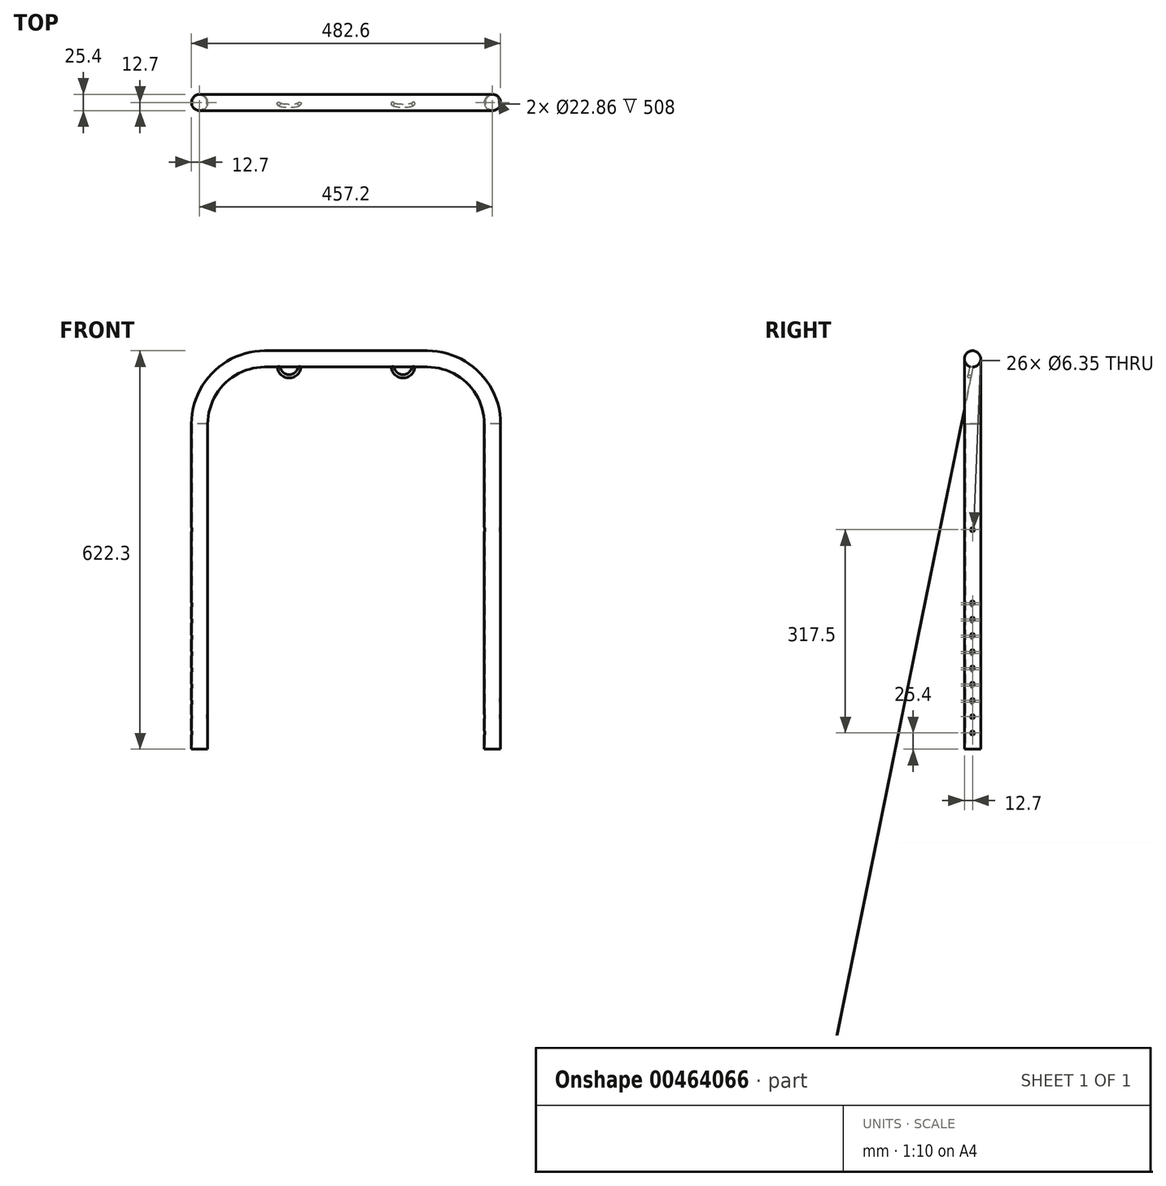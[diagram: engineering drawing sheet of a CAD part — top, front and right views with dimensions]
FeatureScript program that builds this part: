
annotation { "Feature Type Name" : "Feature", "Feature Type Description" : "" }
export const myFeature = defineFeature(function(context is Context, id is Id, definition is map)
    precondition{}
    {
        {
            var Q0;
            Q0=qCreatedBy(makeId("Front.planeOp"),FACE);
            var sketch = newSketch(context, id + "F0", { "sketchPlane" : qUnion([Q0])});
            skLineSegment(sketch, "E0", {"start": v(0, 0) * mm, "end": v(-228.6, 0) * mm});
            skLineSegment(sketch, "E1", {"start": v(-228.6, 0) * mm, "end": v(-228.6, 508) * mm});
            skLineSegment(sketch, "E2", {"start": v(0, 0) * mm, "end": v(0, 609.6) * mm});
            skLineSegment(sketch, "E3", {"start": v(0, 609.6) * mm, "end": v(-127, 609.6) * mm});
            skArc(sketch, "E4", {"start": v(-127, 609.6) * mm, "mid": v(-198.84, 579.84) * mm, "end": v(-228.6, 508) * mm});
            skSolve(sketch);
        }
        {
            var Q0;
            Q0=qCreatedBy(makeId("Top.planeOp"),FACE);
            var sketch = newSketch(context, id + "F1", { "sketchPlane" : qUnion([Q0])});
            skLineSegment(sketch, "E5", {"start": v(0, 0) * mm, "end": v(-228.6, 0) * mm});
            skCircle(sketch, "E6", {"center": v(-228.6, 0) * mm, "radius": 12.7 * mm});
            skSolve(sketch);
        }
        {
            var Q0;
            Q0=makeQuery(id+"F1.imprint","IMPRINT",FACE,{"disambiguationData":[TD([[makeQuery(id+"F1.imprint","IMPRINT",EDGE,{"derivedFrom":sQuery(id+"F1.wireOp",EDGE,"E6")}),1.0]])]});
            var Q1;
            Q1=sQuery(id+"F0.wireOp",EDGE,"E1");
            var Q2;
            Q2=sQuery(id+"F0.wireOp",EDGE,"E4");
            var Q3;
            Q3=sQuery(id+"F0.wireOp",EDGE,"E3");
            sweep(context, id + "F2", {"profiles" : qUnion([Q0]), "path" : qUnion([Q1, Q2, Q3])});
        }
        {
            var Q0;
            Q0=makeQuery(id+"F2.opSweep","SWEPT_BODY",BODY,{"disambiguationData":[OSD([sQuery(id+"F0.wireOp",EDGE,"E3"),sQuery(id+"F1.wireOp",EDGE,"E6")])]});
            var Q1;
            Q1=qCreatedBy(makeId("Right.planeOp"),FACE);
            mirror(context, id + "F3", {"operationType" : NewBodyOperationType.ADD, "entities" : qUnion([Q0]), "mirrorPlane" : qUnion([Q1])});
        }
        {
            var Q0;
            Q0=qCreatedBy(makeId("Right.planeOp"),FACE);
            cPlane(context, id + "F4", {"entities" : qUnion([Q0]), "cplaneType" : CPlaneType.OFFSET, "offset" : 228.6 * mm, "width" : 152.4 * mm, "height" : 152.4 * mm});
        }
        {
            var Q0;
            Q0=qCreatedBy(id+"F4.planeOp",FACE);
            cPlane(context, id + "F5", {"entities" : qUnion([Q0]), "cplaneType" : CPlaneType.OFFSET, "offset" : 6.35 * mm, "oppositeDirection" : true, "width" : 152.4 * mm, "height" : 152.4 * mm});
        }
        {
            var Q0;
            Q0=qCreatedBy(id+"F5.planeOp",FACE);
            var sketch = newSketch(context, id + "F6", { "sketchPlane" : qUnion([Q0])});
            skLineSegment(sketch, "E7", {"start": v(0, 0) * mm, "end": v(0, 50.8) * mm});
            skCircle(sketch, "E8", {"center": v(0, 50.8) * mm, "radius": 3.18 * mm});
            skSolve(sketch);
        }
        {
            var Q0;
            Q0 = qSketchRegion(id + "F6", true);
            extrude(context, id + "F7", {"entities" : qUnion([Q0]), "operationType" : NewBodyOperationType.REMOVE, "oppositeDirection" : true, "depth" : 601.98 * mm, "hasSecondDirection" : true, "secondDirectionOppositeDirection" : false, "secondDirectionDepth" : 101.6 * mm});
        }
        {
            var Q0;
            Q0=qCreatedBy(id+"F4.planeOp",FACE);
            var sketch = newSketch(context, id + "F8", { "sketchPlane" : qUnion([Q0])});
            skLineSegment(sketch, "E9", {"start": v(0, 0) * mm, "end": v(0, 342.9) * mm});
            skCircle(sketch, "E10", {"center": v(0, 342.9) * mm, "radius": 3.18 * mm});
            skSolve(sketch);
        }
        {
            var Q0;
            Q0 = qSketchRegion(id + "F8", true);
            extrude(context, id + "F9", {"entities" : qUnion([Q0]), "operationType" : NewBodyOperationType.REMOVE, "depth" : 19.05 * mm, "hasSecondDirection" : true, "secondDirectionOppositeDirection" : true, "secondDirectionDepth" : 840.74 * mm});
        }
        {
            var Q0;
            Q0=qCreatedBy(id+"F4.planeOp",FACE);
            var sketch = newSketch(context, id + "F10", { "sketchPlane" : qUnion([Q0])});
            skCircle(sketch, "E11", {"center": v(0, 25.4) * mm, "radius": 3.18 * mm});
            skSolve(sketch);
        }
        {
            var Q0;
            Q0 = qSketchRegion(id + "F10", true);
            extrude(context, id + "F11", {"entities" : qUnion([Q0]), "operationType" : NewBodyOperationType.REMOVE, "depth" : 19.05 * mm, "hasSecondDirection" : true, "secondDirectionOppositeDirection" : true, "secondDirectionDepth" : 693.42 * mm, "offsetDistance" : 25.4 * mm});
        }
        {
            var Q0;
            Q0=qCreatedBy(makeId("Top.planeOp"),FACE);
            cPlane(context, id + "F12", {"entities" : qUnion([Q0]), "cplaneType" : CPlaneType.OFFSET, "offset" : 596.9 * mm, "width" : 152.4 * mm, "height" : 152.4 * mm});
        }
        {
            var Q0;
            Q0=qCreatedBy(makeId("Right.planeOp"),FACE);
            var sketch = newSketch(context, id + "F13", { "sketchPlane" : qUnion([Q0])});
            skLineSegment(sketch, "E12", {"start": v(0, 594.75) * mm, "end": v(-58.05, 606.55) * mm});
            skLineSegment(sketch, "E13", {"start": v(0, 594.75) * mm, "end": v(13.15, 659.45) * mm});
            skSolve(sketch);
        }
        {
            var Q0;
            Q0=qCreatedBy(id+"F12.planeOp",FACE);
            var Q1;
            Q1=sQuery(id+"F13.wireOp",EDGE,"E12");
            cPlane(context, id + "F14", {"entities" : qUnion([Q0, Q1]), "cplaneType" : CPlaneType.LINE_ANGLE, "offset" : 25.4 * mm, "angle" : 0 * degree, "width" : 152.4 * mm, "height" : 152.4 * mm});
        }
        {
            var Q0;
            Q0=qCreatedBy(makeId("Front.planeOp"),FACE);
            var Q1;
            Q1=sQuery(id+"F13.wireOp",EDGE,"E13");
            cPlane(context, id + "F15", {"entities" : qUnion([Q0, Q1]), "cplaneType" : CPlaneType.LINE_ANGLE, "offset" : 25.4 * mm, "angle" : 0 * degree, "width" : 152.4 * mm, "height" : 152.4 * mm});
        }
        {
            var Q0;
            Q0=qCreatedBy(id+"F15.planeOp",FACE);
            var sketch = newSketch(context, id + "F16", { "sketchPlane" : qUnion([Q0])});
            skLineSegment(sketch, "E14", {"start": v(0, 585.75) * mm, "end": v(88.9, 585.75) * mm});
            skLineSegment(sketch, "E15", {"start": v(0, 585.75) * mm, "end": v(-88.9, 585.75) * mm});
            skCircle(sketch, "E16", {"center": v(88.9, 585.75) * mm, "radius": 15.88 * mm});
            skCircle(sketch, "E17", {"center": v(-88.9, 585.75) * mm, "radius": 15.88 * mm});
            skLineSegment(sketch, "E18", {"start": v(0, 585.75) * mm, "end": v(73.03, 585.75) * mm});
            skSolve(sketch);
        }
        {
            var Q0;
            Q0=qCreatedBy(id+"F14.planeOp",FACE);
            var sketch = newSketch(context, id + "F17", { "sketchPlane" : qUnion([Q0])});
            skLineSegment(sketch, "E19", {"start": v(0, 120.77) * mm, "end": v(-73.03, 120.77) * mm});
            skLineSegment(sketch, "E20", {"start": v(0, 120.77) * mm, "end": v(73.03, 120.77) * mm});
            skCircle(sketch, "E21", {"center": v(-73.03, 120.77) * mm, "radius": 2.54 * mm});
            skCircle(sketch, "E22", {"center": v(73.03, 120.77) * mm, "radius": 2.54 * mm});
            skSolve(sketch);
        }
        {
            var Q0;
            Q0=makeQuery(id+"F17.imprint","IMPRINT",FACE,{"disambiguationData":[TD([[makeQuery(id+"F17.imprint","IMPRINT",EDGE,{"derivedFrom":sQuery(id+"F17.wireOp",EDGE,"E21")}),1.0]])]});
            var Q1;
            Q1=sQuery(id+"F16.wireOp",EDGE,"E16");
            sweep(context, id + "F18", {"operationType" : NewBodyOperationType.ADD, "profiles" : qUnion([Q0]), "path" : qUnion([Q1])});
        }
        {
            var Q0;
            Q0=makeQuery(id+"F17.imprint","IMPRINT",FACE,{"disambiguationData":[TD([[makeQuery(id+"F17.imprint","IMPRINT",EDGE,{"derivedFrom":sQuery(id+"F17.wireOp",EDGE,"E22")}),1.0]])]});
            var Q1;
            Q1=sQuery(id+"F16.wireOp",EDGE,"E17");
            sweep(context, id + "F19", {"operationType" : NewBodyOperationType.ADD, "profiles" : qUnion([Q0]), "path" : qUnion([Q1])});
        }
        {
            var Q0;
            Q0=qCreatedBy(makeId("Top.planeOp"),FACE);
            var sketch = newSketch(context, id + "F20", { "sketchPlane" : qUnion([Q0])});
            skLineSegment(sketch, "E23", {"start": v(0, 0) * mm, "end": v(228.6, 0) * mm});
            skCircle(sketch, "E24", {"center": v(228.6, 0) * mm, "radius": 11.43 * mm});
            skLineSegment(sketch, "E25", {"start": v(0, 0) * mm, "end": v(0, 93.67) * mm});
            skCircle(sketch, "E26.MirrorC", {"center": v(-228.6, 0) * mm, "radius": 11.43 * mm});
            skSolve(sketch);
        }
        {
            var Q0;
            Q0 = qSketchRegion(id + "F20", true);
            extrude(context, id + "F21", {"entities" : qUnion([Q0]), "operationType" : NewBodyOperationType.REMOVE, "depth" : 508 * mm, "offsetDistance" : 25.4 * mm});
        }
        {
            var Q0;
            Q0=qCreatedBy(id+"F4.planeOp",FACE);
            var sketch = newSketch(context, id + "F22", { "sketchPlane" : qUnion([Q0])});
            skLineSegment(sketch, "E27", {"start": v(0, 0) * mm, "end": v(0, 76.2) * mm});
            skLineSegment(sketch, "E28", {"start": v(0, 76.2) * mm, "end": v(0, 101.6) * mm});
            skLineSegment(sketch, "E29", {"start": v(0, 101.6) * mm, "end": v(0, 127) * mm});
            skLineSegment(sketch, "E30", {"start": v(0, 127) * mm, "end": v(0, 152.4) * mm});
            skLineSegment(sketch, "E31", {"start": v(0, 152.4) * mm, "end": v(0, 177.8) * mm});
            skLineSegment(sketch, "E32", {"start": v(0, 177.8) * mm, "end": v(0, 203.2) * mm});
            skLineSegment(sketch, "E33", {"start": v(0, 203.2) * mm, "end": v(0, 228.6) * mm});
            skCircle(sketch, "E34", {"center": v(0, 76.2) * mm, "radius": 3.18 * mm});
            skCircle(sketch, "E35", {"center": v(0, 101.6) * mm, "radius": 3.18 * mm});
            skCircle(sketch, "E36", {"center": v(0, 127) * mm, "radius": 3.18 * mm});
            skCircle(sketch, "E37", {"center": v(0, 152.4) * mm, "radius": 3.18 * mm});
            skCircle(sketch, "E38", {"center": v(0, 177.8) * mm, "radius": 3.18 * mm});
            skCircle(sketch, "E39", {"center": v(0, 203.2) * mm, "radius": 3.18 * mm});
            skCircle(sketch, "E40", {"center": v(0, 228.6) * mm, "radius": 3.18 * mm});
            skSolve(sketch);
        }
        {
            var Q0;
            Q0 = qSketchRegion(id + "F22", true);
            extrude(context, id + "F23", {"entities" : qUnion([Q0]), "operationType" : NewBodyOperationType.REMOVE, "depth" : 25.4 * mm, "offsetDistance" : 25.4 * mm});
        }
        {
            var Q0;
            Q0=qCreatedBy(makeId("Right.planeOp"),FACE);
            cPlane(context, id + "F24", {"entities" : qUnion([Q0]), "cplaneType" : CPlaneType.OFFSET, "offset" : 228.6 * mm, "oppositeDirection" : true, "width" : 152.4 * mm, "height" : 152.4 * mm});
        }
        {
            var Q0;
            Q0=qCreatedBy(id+"F24.planeOp",FACE);
            var sketch = newSketch(context, id + "F25", { "sketchPlane" : qUnion([Q0])});
            skLineSegment(sketch, "E41", {"start": v(0, -2.89) * mm, "end": v(0, 73.31) * mm});
            skLineSegment(sketch, "E42", {"start": v(0, 73.31) * mm, "end": v(0, 98.71) * mm});
            skLineSegment(sketch, "E43", {"start": v(0, 98.71) * mm, "end": v(0, 124.11) * mm});
            skLineSegment(sketch, "E44", {"start": v(0, 124.11) * mm, "end": v(0, 149.51) * mm});
            skLineSegment(sketch, "E45", {"start": v(0, 149.51) * mm, "end": v(0, 174.91) * mm});
            skLineSegment(sketch, "E46", {"start": v(0, 174.91) * mm, "end": v(0, 200.31) * mm});
            skLineSegment(sketch, "E47", {"start": v(0, 200.31) * mm, "end": v(0, 225.71) * mm});
            skCircle(sketch, "E48", {"center": v(0, 225.71) * mm, "radius": 3.18 * mm});
            skCircle(sketch, "E49", {"center": v(0, 200.31) * mm, "radius": 3.17 * mm});
            skCircle(sketch, "E50", {"center": v(0, 174.91) * mm, "radius": 3.18 * mm});
            skCircle(sketch, "E51", {"center": v(0, 149.51) * mm, "radius": 3.18 * mm});
            skCircle(sketch, "E52", {"center": v(0, 124.11) * mm, "radius": 3.18 * mm});
            skCircle(sketch, "E53", {"center": v(0, 98.71) * mm, "radius": 3.18 * mm});
            skCircle(sketch, "E54", {"center": v(0, 73.31) * mm, "radius": 3.18 * mm});
            skSolve(sketch);
        }
        {
            var Q0;
            Q0 = qSketchRegion(id + "F25", true);
            extrude(context, id + "F26", {"entities" : qUnion([Q0]), "operationType" : NewBodyOperationType.REMOVE, "oppositeDirection" : true, "depth" : 25.4 * mm, "offsetDistance" : 25.4 * mm});
        }
    });
